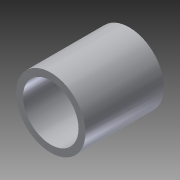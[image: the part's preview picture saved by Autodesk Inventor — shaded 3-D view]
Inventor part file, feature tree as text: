
AUTODESK INVENTOR PART (.ipt)
format: ipt  version: 2014 SP1 (Build 180222100, 222)  size: 97,792 bytes
history: native  units: in
note: dims shown in document units (in); Inventor stores cm internally (conversion verified against a paired STEP export)
features: extrude x1, sketch x1
ambient origin geometry x8: Origin, YZ Plane, XZ Plane, XY Plane, X Axis, Y Axis, Z Axis, Center Point
bodies: Solid1 (feature_tree)
feature tree (2):
  extrude  "Extrusion1"  Depth=0.707in
  sketch  "Sketch1"  dims[d0=0.5in d1=0.625in d2=0.707in d3=0.0in]
